# Revit family: MECON Turbo-Lux 2
name_source: partatom
category: Rohrzubehör
units: mm (PartAtom-declared; Revit-internal decimal feet)

## family parameters
Arbeitsebenenbasiert = Nein
Beim Laden mit Abzugskörper schneiden = Nein
Bemaßung runder Anschluss = Radius verwenden
Gemeinsam genutzt = Nein
Immer vertikal = Ja
OmniClass-Nummer = 23.60.10.17
OmniClass-Titel = Flow Meters
Teiletyp = Ventil - Zerlegung in

## types (5) — shared parameters
Approval = VdS
Black = Metal - black
Build in Length = 55 mm  [stored 0.180446 ft]
Dark Grey = Metal - RAL5015
Delivery Time = in stock
Download Test Certificate = https://download.mecon.de
Glass = Glass-
Grey = Metal - grey
Hersteller = MECON GmbH, Röntgenstraße 105, 50169 Kerpen, Germany
IfcExportAs = IfcFlowMeter
IfcExportType = FLOWMETER
Index = 20200330
Operating Manual = https://www.mecon.de
URL = https://www.mecon.de
VdS Approval = https://www.mecon.de
Website Product = https://www.mecon.de
iFM = Nein
iLPCB = Nein
iVdS = Ja
zero-valued in all types: Vorgabe-Ansicht

## per-type parameters (varying)
| type | Flow Range | Modell | Nominal_Diameter | Nominal_Radius | Order Code | iD2 | iR1 |
| DN 80 (Qv 0,42-2,1 m³/min) | 0.42 - 2.1 m³/min | DN 80 (Qv: 0,42 - 2,1 m³/min) | 80 mm | 40 mm | 7ME5834-1AA00-0AA0 | 110 mm | 71.5 mm |
| DN 100 (Qv 0,6-3,0 m³/min) | 0.6 - 3.0 m³/min | DN 100 (Qv: 0,6 - 3,0 m³/min) | 100 mm | 50 mm | 7ME5834-2AA00-0AA0 | 120 mm  [stored 0.393701 ft] | 81.5 mm  [stored 0.267388 ft] |
| DN 150 (Qv 1,2-6,0 m³/min) | 1.2 - 6.0 m³/min | DN 150 (Qv: 1,2 - 6,0 m³/min) | 150 mm | 75 mm | 7ME5834-3AA00-0AA0 | 145 mm  [stored 0.475722 ft] | 106.5 mm  [stored 0.349409 ft] |
| DN 200 (Qv 2,4-12,0 m³/min) | 2.4 - 12.0 m³/min | DN 200 (Qv: 2,4 - 12,0 m³/min) | 200 mm | 100 mm | 7ME5834-4AA00-0AA0 | 170 mm | 131.5 mm  [stored 0.43143 ft] |
| DN 250 (Qv 3,6-18,0 m³/min) | 3.6 - 18.0 m³/min | DN 250 (Qv: 3,6 - 18,0 m³/min) | 250 mm | 125 mm | 7ME5834-5AA00-0AA0 | 195 mm | 156.5 mm |

note: column(s) folded — value = type name in every type: Typenkommentare

note: [stored X ft] marks values corroborated as IEEE doubles in the binary element streams (Revit-internal decimal feet)
